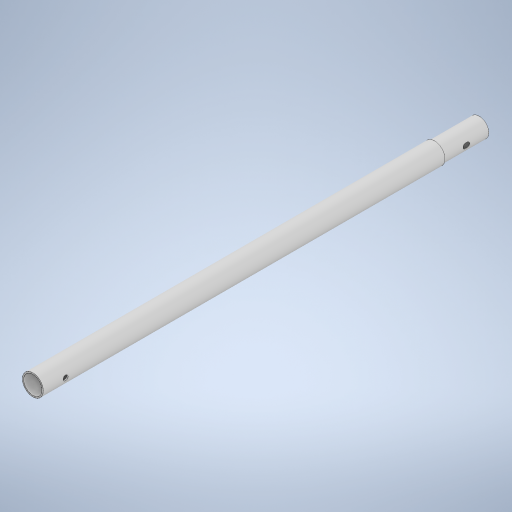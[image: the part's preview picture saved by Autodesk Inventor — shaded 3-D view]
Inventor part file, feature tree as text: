
AUTODESK INVENTOR PART (.ipt)
format: ipt  version: 2024 (Build 280153000, 153)  size: 290,816 bytes
history: native  units: mm
features: sketch x6, extrude x5, plane x2, hole x1
ambient origin geometry x8: Origin, YZ Plane, XZ Plane, XY Plane, X Axis, Y Axis, Z Axis, Center Point
bodies: Solid1 (feature_tree)
feature tree (14):
  extrude  "Extrusion1"  Depth=900.0mm TaperAngle=0.0deg
  extrude  "Extrusion2"  Depth=900.0mm TaperAngle=0.0deg
  extrude  "Extrusion3"  Depth=100.0mm TaperAngle=0.0deg
  extrude  "Extrusion4"  Depth=100.0mm TaperAngle=0.0deg
  plane  "Work Plane1"
  extrude  "Extrusion5"  Depth=11.0mm
  hole  "Hole1"  [1 undecoded]
  plane  "Work Plane2"
  sketch  "Sketch1"  dims[d0=47.0mm d1=900.0mm d2=0.0mm]
  sketch  "Sketch2"  dims[d3=41.0mm d4=900.0mm d5=0.0mm]
  sketch  "Sketch3"  dims[d6=43.0mm d7=100.0mm d8=0.0mm]
  sketch  "Sketch4"  dims[d9=41.0mm d10=100.0mm d11=0.0mm]
  sketch  "Sketch5"  dims[d12=23.5mm d13=11.0mm]
  sketch  "Sketch6"  dims[d14=48.0mm d15=11.0mm d16=52.0mm d17=11.0mm d18=47.0mm d19=0.0mm d20=11.0mm d21=50.0mm d22=11.0mm d23=6.0mm d24=4.0mm d25=2.0mm d26=90.0deg d27=47.0mm d28=0.0mm d29=23.25mm]
note: 1 required parameter value undecoded (feature->parameter linkage not recoverable at this tier; creation-order binding heuristic only, values carry confidence <= 0.55)
